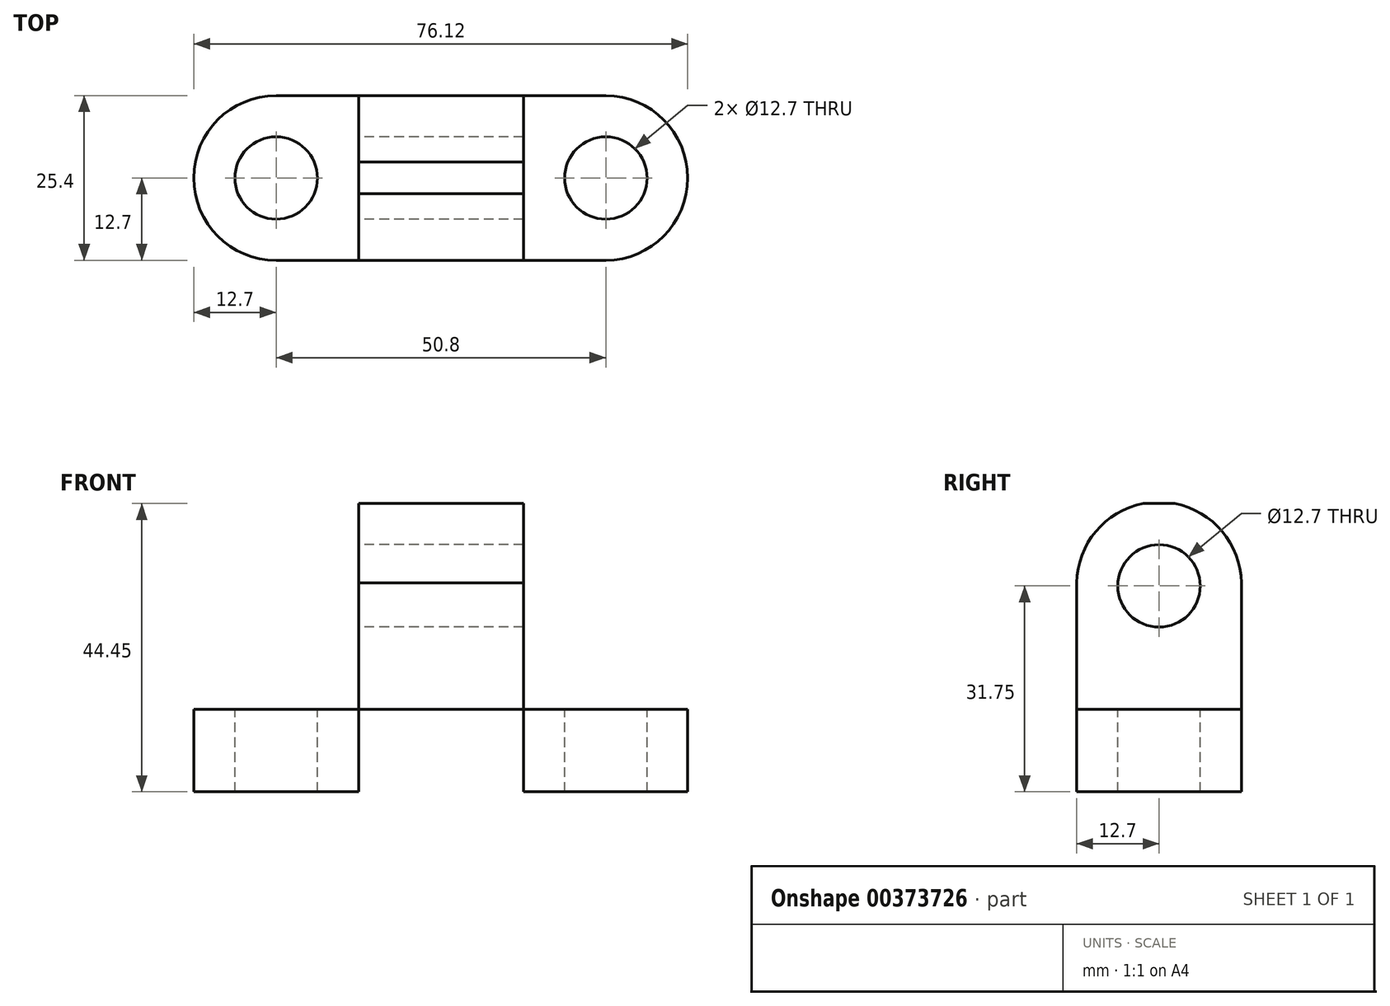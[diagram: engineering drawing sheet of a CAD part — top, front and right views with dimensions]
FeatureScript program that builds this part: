
annotation { "Feature Type Name" : "Feature", "Feature Type Description" : "" }
export const myFeature = defineFeature(function(context is Context, id is Id, definition is map)
    precondition{}
    {
        {
            var Q0;
            Q0=qCreatedBy(makeId("Front.planeOp"),FACE);
            var sketch = newSketch(context, id + "F0", { "sketchPlane" : qUnion([Q0])});
            skLineSegment(sketch, "E0.bottom", {"start": v(0, 0) * mm, "end": v(76.2, 0) * mm});
            skLineSegment(sketch, "E0.top", {"start": v(0, 12.7) * mm, "end": v(76.2, 12.7) * mm});
            skLineSegment(sketch, "E0.left", {"start": v(0, 0) * mm, "end": v(0, 12.7) * mm});
            skLineSegment(sketch, "E0.right", {"start": v(76.2, 0) * mm, "end": v(76.2, 12.7) * mm});
            skLineSegment(sketch, "E1.bottom", {"start": v(25.4, 0) * mm, "end": v(50.8, 0) * mm});
            skLineSegment(sketch, "E1.top", {"start": v(25.4, 44.45) * mm, "end": v(50.8, 44.45) * mm});
            skLineSegment(sketch, "E1.left", {"start": v(25.4, 0) * mm, "end": v(25.4, 44.45) * mm});
            skLineSegment(sketch, "E1.right", {"start": v(50.8, 0) * mm, "end": v(50.8, 44.45) * mm});
            skSolve(sketch);
        }
        {
            var Q0;
            {var subQ0=sQuery(id+"F0.wireOp",EDGE,"E0.left");Q0=makeQuery(id+"F0.imprint","IMPRINT",FACE,{"disambiguationData":[TD([[makeQuery(id+"F0.imprint","IMPRINT",EDGE,{"derivedFrom":subQ0}),-1.0]])]});}
            var Q1;
            {var subQ5=sQuery(id+"F0.wireOp",EDGE,"E1.bottom");Q1=makeQuery(id+"F0.imprint","IMPRINT",FACE,{"disambiguationData":[TD([[makeQuery(id+"F0.imprint","IMPRINT",EDGE,{"derivedFrom":subQ5}),1.0]])]});}
            var Q2;
            {var subQ0=sQuery(id+"F0.wireOp",EDGE,"E0.right");Q2=makeQuery(id+"F0.imprint","IMPRINT",FACE,{"disambiguationData":[TD([[makeQuery(id+"F0.imprint","IMPRINT",EDGE,{"derivedFrom":subQ0}),1.0]])]});}
            var Q3;
            {var subQ5=sQuery(id+"F0.wireOp",EDGE,"E1.top");Q3=makeQuery(id+"F0.imprint","IMPRINT",FACE,{"disambiguationData":[TD([[makeQuery(id+"F0.imprint","IMPRINT",EDGE,{"derivedFrom":subQ5}),-1.0]])]});}
            extrude(context, id + "F1", {"entities" : qUnion([Q0, Q1, Q2, Q3]), "depth" : 25.4 * mm});
        }
        {
            var Q0;
            Q0=makeQuery(id+"F1.opExtrude","SWEPT_FACE",FACE,{"disambiguationData":[OSD([sQuery(id+"F0.wireOp",EDGE,"E1.left")])]});
            var sketch = newSketch(context, id + "F2", { "sketchPlane" : qUnion([Q0])});
            skCircle(sketch, "E2", {"center": v(12.7, 31.75) * mm, "radius": 6.35 * mm});
            skArc(sketch, "E3", {"start": v(25.4, 31.75) * mm, "mid": v(12.7, 44.69) * mm, "end": v(0, 31.75) * mm});
            skSolve(sketch);
        }
        {
            var Q0;
            Q0=makeQuery(id+"F2.imprint","IMPRINT",FACE,{"disambiguationData":[TD([[makeQuery(id+"F2.imprint","IMPRINT",EDGE,{"derivedFrom":sQuery(id+"F2.wireOp",EDGE,"E2")}),1.0]])]});
            var Q1;
            {var subQ0=sQuery(id+"F2.wireOp",EDGE,"E3");var subQ1=sQuery(id+"F0.wireOp",EDGE,"E1.left");var subQ4=makeQuery(id+"F1.opExtrude","CAP_EDGE",EDGE,{"disambiguationData":[OSD([subQ1])],"isStart":true});var subQ5=makeQuery(id+"F2.imprint","INTERSECT",VERTEX,{"disambiguationData":[OD(1.0)],"derivedFrom":[subQ4,subQ0]});Q1=makeQuery(id+"F2.imprint","IMPRINT",FACE,{"disambiguationData":[TD([[makeQuery(id+"F2.imprint","IMPRINT",EDGE,{"disambiguationData":[TD([[subQ5,1.0]])],"derivedFrom":subQ0}),-1.0]])]});}
            var Q2;
            {var subQ0=sQuery(id+"F2.wireOp",EDGE,"E3");var subQ1=sQuery(id+"F0.wireOp",EDGE,"E1.left");var subQ2=makeQuery(id+"F1.opExtrude","CAP_EDGE",EDGE,{"disambiguationData":[OSD([subQ1])],"isStart":false});var subQ3=makeQuery(id+"F2.imprint","INTERSECT",VERTEX,{"disambiguationData":[OD(1.0)],"derivedFrom":[subQ2,subQ0]});Q2=makeQuery(id+"F2.imprint","IMPRINT",FACE,{"disambiguationData":[TD([[makeQuery(id+"F2.imprint","IMPRINT",EDGE,{"disambiguationData":[TD([[subQ3,-1.0]])],"derivedFrom":subQ0}),-1.0]])]});}
            extrude(context, id + "F3", {"entities" : qUnion([Q0, Q1, Q2]), "operationType" : NewBodyOperationType.REMOVE, "oppositeDirection" : true, "depth" : 25.4 * mm});
        }
        {
            var Q0;
            {var subQ0=sQuery(id+"F0.wireOp",EDGE,"E0.top");Q0=makeQuery(id+"F1.opExtrude","SWEPT_FACE",FACE,{"disambiguationData":[OSD([subQ0]),TDD([makeQuery(id+"F0.imprint","IMPRINT",EDGE,{"disambiguationData":[TD([[makeQuery(id+"F0.imprint","INTERSECT",VERTEX,{"derivedFrom":[subQ0,sQuery(id+"F0.wireOp",EDGE,"E0.left")]}),-1.0]])],"derivedFrom":subQ0})])]});}
            var sketch = newSketch(context, id + "F4", { "sketchPlane" : qUnion([Q0])});
            skCircle(sketch, "E4", {"center": v(12.7, -12.7) * mm, "radius": 6.35 * mm});
            skPoint(sketch, "E4.centerSnap0", {"position": v(0, -12.7) * mm});
            skCircle(sketch, "E5", {"center": v(63.5, -12.7) * mm, "radius": 6.35 * mm});
            skArc(sketch, "E6", {"start": v(12.7, 0) * mm, "mid": v(0, -12.7) * mm, "end": v(12.7, -25.4) * mm});
            skArc(sketch, "E7", {"start": v(63.5, -25.4) * mm, "mid": v(75.9, -12.7) * mm, "end": v(63.5, 0) * mm});
            skSolve(sketch);
        }
        {
            var Q0;
            Q0=makeQuery(id+"F4.imprint","IMPRINT",FACE,{"disambiguationData":[TD([[makeQuery(id+"F4.imprint","IMPRINT",EDGE,{"derivedFrom":sQuery(id+"F4.wireOp",EDGE,"E4")}),1.0]])]});
            var Q1;
            Q1=makeQuery(id+"F4.imprint","IMPRINT",FACE,{"disambiguationData":[TD([[makeQuery(id+"F4.imprint","IMPRINT",EDGE,{"derivedFrom":sQuery(id+"F4.wireOp",EDGE,"E5")}),1.0]])]});
            var Q2;
            {var subQ0=sQuery(id+"F4.wireOp",EDGE,"E6");var subQ1=sQuery(id+"F0.wireOp",EDGE,"E0.left");var subQ2=sQuery(id+"F0.wireOp",EDGE,"E0.top");var subQ5=makeQuery(id+"F1.opExtrude","SWEPT_EDGE",EDGE,{"disambiguationData":[OSD([subQ2,subQ1])]});var subQ6=makeQuery(id+"F4.imprint","INTERSECT",VERTEX,{"derivedFrom":[subQ5,subQ0]});Q2=makeQuery(id+"F4.imprint","IMPRINT",FACE,{"disambiguationData":[TD([[makeQuery(id+"F4.imprint","IMPRINT",EDGE,{"disambiguationData":[TD([[subQ6,1.0]])],"derivedFrom":subQ0}),-1.0]])]});}
            var Q3;
            {var subQ0=sQuery(id+"F4.wireOp",EDGE,"E6");var subQ1=sQuery(id+"F0.wireOp",EDGE,"E0.left");var subQ2=sQuery(id+"F0.wireOp",EDGE,"E0.top");var subQ5=makeQuery(id+"F1.opExtrude","SWEPT_EDGE",EDGE,{"disambiguationData":[OSD([subQ2,subQ1])]});var subQ6=makeQuery(id+"F4.imprint","INTERSECT",VERTEX,{"derivedFrom":[subQ5,subQ0]});Q3=makeQuery(id+"F4.imprint","IMPRINT",FACE,{"disambiguationData":[TD([[makeQuery(id+"F4.imprint","IMPRINT",EDGE,{"disambiguationData":[TD([[subQ6,-1.0]])],"derivedFrom":subQ0}),-1.0]])]});}
            extrude(context, id + "F5", {"entities" : qUnion([Q0, Q1, Q2, Q3]), "operationType" : NewBodyOperationType.REMOVE, "oppositeDirection" : true, "depth" : 25.4 * mm});
        }
        {
            var Q0;
            {var subQ0=sQuery(id+"F0.wireOp",EDGE,"E0.top");Q0=makeQuery(id+"F1.opExtrude","SWEPT_FACE",FACE,{"disambiguationData":[OSD([subQ0]),TDD([makeQuery(id+"F0.imprint","IMPRINT",EDGE,{"disambiguationData":[TD([[makeQuery(id+"F0.imprint","INTERSECT",VERTEX,{"derivedFrom":[subQ0,sQuery(id+"F0.wireOp",EDGE,"E0.right")]}),1.0]])],"derivedFrom":subQ0})])]});}
            var sketch = newSketch(context, id + "F6", { "sketchPlane" : qUnion([Q0])});
            skArc(sketch, "E8", {"start": v(63.5, -25.4) * mm, "mid": v(76.12, -12.7) * mm, "end": v(63.5, 0) * mm});
            skSolve(sketch);
        }
        {
            var Q0;
            {var subQ0=sQuery(id+"F6.wireOp",EDGE,"E8");Q0=makeQuery(id+"F6.imprint","IMPRINT",FACE,{"disambiguationData":[TD([[makeQuery(id+"F6.imprint","IMPRINT",EDGE,{"derivedFrom":subQ0}),-1.0]])]});}
            extrude(context, id + "F7", {"entities" : qUnion([Q0]), "operationType" : NewBodyOperationType.REMOVE, "oppositeDirection" : true, "depth" : 25.4 * mm});
        }
    });
